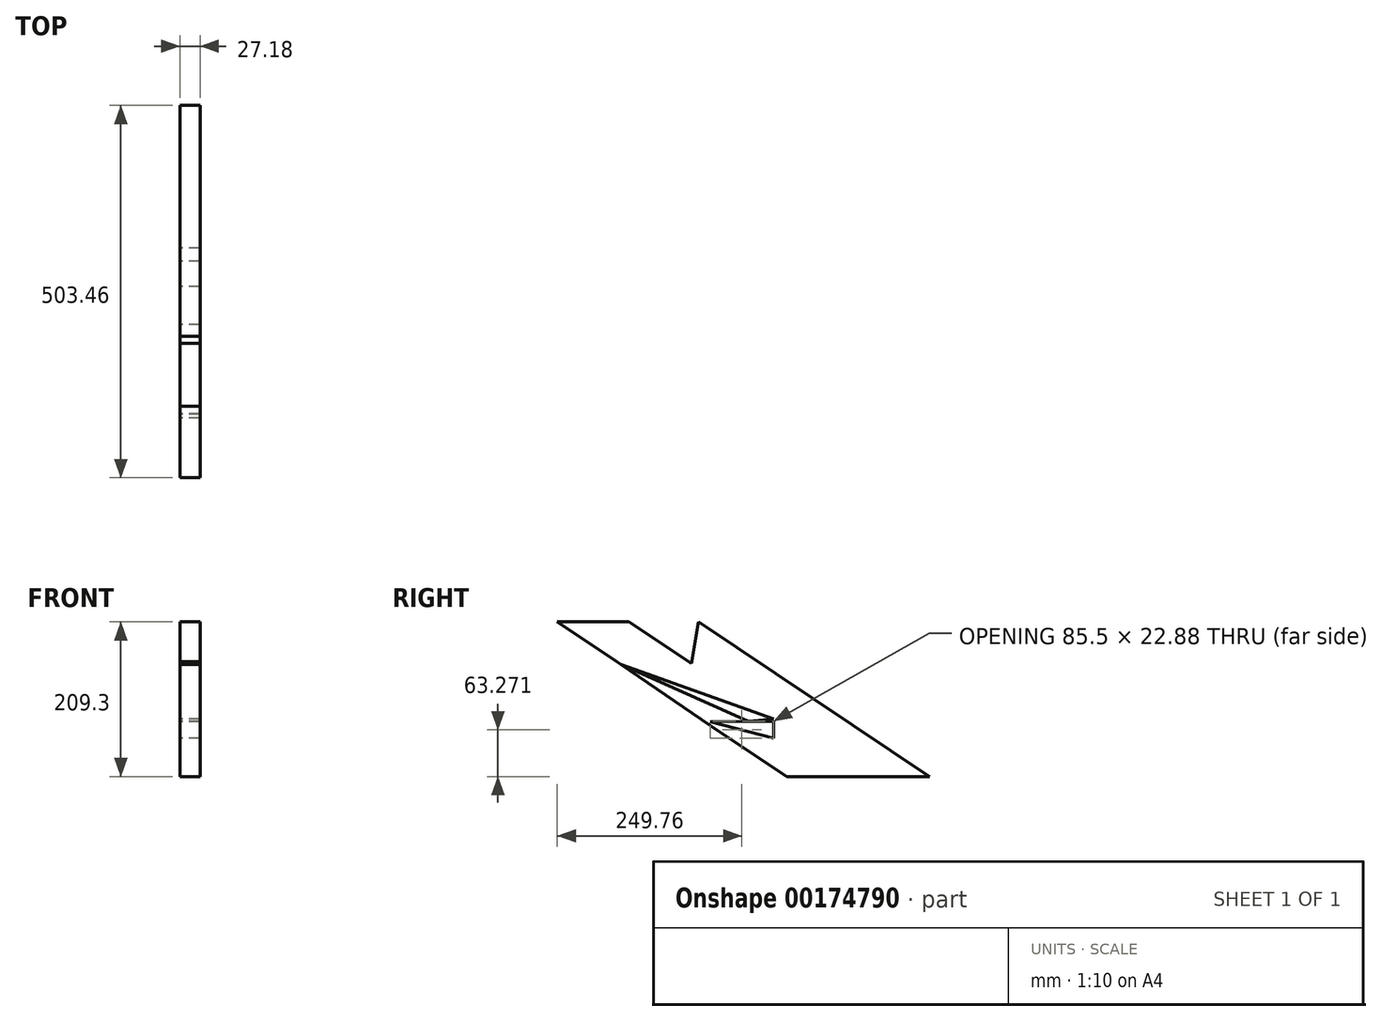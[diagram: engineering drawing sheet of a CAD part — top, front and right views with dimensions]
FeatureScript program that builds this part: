
annotation { "Feature Type Name" : "Feature", "Feature Type Description" : "" }
export const myFeature = defineFeature(function(context is Context, id is Id, definition is map)
    precondition{}
    {
        {
            var Q0;
            Q0=qCreatedBy(makeId("Right.planeOp"),FACE);
            var sketch = newSketch(context, id + "F0", { "sketchPlane" : qUnion([Q0])});
            skLineSegment(sketch, "E0", {"start": v(-206.47, 74.06) * mm, "end": v(-292.5, 131.66) * mm});
            skLineSegment(sketch, "E1", {"start": v(-292.5, 131.66) * mm, "end": v(-195.72, 131.66) * mm});
            skLineSegment(sketch, "E2", {"start": v(-195.72, 131.66) * mm, "end": v(-111.11, 75.01) * mm});
            skLineSegment(sketch, "E3", {"start": v(-111.11, 75.01) * mm, "end": v(-206.47, 74.06) * mm});
            skLineSegment(sketch, "E4", {"start": v(-206.47, 74.06) * mm, "end": v(-195.72, 131.66) * mm});
            skLineSegment(sketch, "E5", {"start": v(-292.5, 131.66) * mm, "end": v(-111.11, 75.01) * mm});
            skLineSegment(sketch, "E6", {"start": v(-195.72, 131.66) * mm, "end": v(-101.62, 131.66) * mm});
            skLineSegment(sketch, "E7", {"start": v(-101.62, 131.66) * mm, "end": v(-111.11, 75.01) * mm});
            skLineSegment(sketch, "E8", {"start": v(-110.23, 73.12) * mm, "end": v(-16.55, 74.06) * mm});
            skLineSegment(sketch, "E9", {"start": v(-16.55, 74.06) * mm, "end": v(0, 0) * mm});
            skLineSegment(sketch, "E10", {"start": v(0, 0) * mm, "end": v(-206.47, 74.06) * mm});
            skLineSegment(sketch, "E11", {"start": v(-206.47, 74.06) * mm, "end": v(-33.87, -2.93) * mm});
            skLineSegment(sketch, "E12", {"start": v(-33.87, -2.93) * mm, "end": v(0, 0) * mm});
            skLineSegment(sketch, "E13", {"start": v(0, -2.93) * mm, "end": v(-85.5, -3.79) * mm});
            skLineSegment(sketch, "E14", {"start": v(-85.5, -3.79) * mm, "end": v(0, -25.8) * mm});
            skLineSegment(sketch, "E15", {"start": v(0, -25.8) * mm, "end": v(0, -2.93) * mm});
            skLineSegment(sketch, "E16", {"start": v(-101.62, 131.66) * mm, "end": v(210.95, -77.64) * mm});
            skLineSegment(sketch, "E17", {"start": v(210.95, -77.64) * mm, "end": v(0, 0) * mm});
            skLineSegment(sketch, "E18", {"start": v(0, -25.8) * mm, "end": v(17.74, -77.64) * mm});
            skLineSegment(sketch, "E19", {"start": v(17.74, -77.64) * mm, "end": v(210.95, -77.64) * mm});
            skLineSegment(sketch, "E20", {"start": v(-85.5, -3.79) * mm, "end": v(-211.78, 77.6) * mm});
            skLineSegment(sketch, "E21", {"start": v(-211.78, 77.6) * mm, "end": v(-348.92, 169.44) * mm});
            skLineSegment(sketch, "E22", {"start": v(-348.92, 169.44) * mm, "end": v(-101.62, 131.66) * mm});
            skLineSegment(sketch, "E23", {"start": v(-85.5, -8.3) * mm, "end": v(17.74, -77.64) * mm});
            skLineSegment(sketch, "E24", {"start": v(-85.5, -8.3) * mm, "end": v(-206.47, 74.06) * mm});
            skLineSegment(sketch, "E25", {"start": v(-155.4, 169.44) * mm, "end": v(-348.92, 169.44) * mm});
            skLineSegment(sketch, "E26", {"start": v(-155.4, 169.44) * mm, "end": v(-101.62, 131.66) * mm});
            skSolve(sketch);
        }
        {
            var Q0;
            {var subQ0=sQuery(id+"F0.wireOp",EDGE,"E2");Q0=makeQuery(id+"F0.imprint","IMPRINT",FACE,{"disambiguationData":[TD([[makeQuery(id+"F0.imprint","IMPRINT",EDGE,{"derivedFrom":subQ0}),-1.0]])]});}
            var Q1;
            {var subQ4=sQuery(id+"F0.wireOp",EDGE,"E7");Q1=makeQuery(id+"F0.imprint","IMPRINT",FACE,{"disambiguationData":[TD([[makeQuery(id+"F0.imprint","IMPRINT",EDGE,{"derivedFrom":subQ4}),1.0]])]});}
            var Q2;
            {var subQ3=sQuery(id+"F0.wireOp",EDGE,"E20");var subQ5=sQuery(id+"F0.wireOp",EDGE,"E4");var subQ6=makeQuery(id+"F0.imprint","INTERSECT",VERTEX,{"derivedFrom":[subQ5,subQ3]});Q2=makeQuery(id+"F0.imprint","IMPRINT",FACE,{"disambiguationData":[TD([[makeQuery(id+"F0.imprint","IMPRINT",EDGE,{"disambiguationData":[TD([[subQ6,-1.0]])],"derivedFrom":subQ5}),-1.0]])]});}
            var Q3;
            {var subQ1=sQuery(id+"F0.wireOp",EDGE,"E14");Q3=makeQuery(id+"F0.imprint","IMPRINT",FACE,{"disambiguationData":[TD([[makeQuery(id+"F0.imprint","IMPRINT",EDGE,{"derivedFrom":subQ1}),-1.0]])]});}
            var Q4;
            {var subQ1=sQuery(id+"F0.wireOp",EDGE,"E12");Q4=makeQuery(id+"F0.imprint","IMPRINT",FACE,{"disambiguationData":[TD([[makeQuery(id+"F0.imprint","IMPRINT",EDGE,{"derivedFrom":subQ1}),-1.0]])]});}
            var Q5;
            {var subQ0=sQuery(id+"F0.wireOp",EDGE,"E20");var subQ1=sQuery(id+"F0.wireOp",EDGE,"E4");var subQ2=makeQuery(id+"F0.imprint","INTERSECT",VERTEX,{"derivedFrom":[subQ1,subQ0]});Q5=makeQuery(id+"F0.imprint","IMPRINT",FACE,{"disambiguationData":[TD([[makeQuery(id+"F0.imprint","IMPRINT",EDGE,{"disambiguationData":[TD([[subQ2,-1.0]])],"derivedFrom":subQ1}),1.0]])]});}
            var Q6;
            {var subQ0=sQuery(id+"F0.wireOp",EDGE,"E1");Q6=makeQuery(id+"F0.imprint","IMPRINT",FACE,{"disambiguationData":[TD([[makeQuery(id+"F0.imprint","IMPRINT",EDGE,{"derivedFrom":subQ0}),-1.0]])]});}
            extrude(context, id + "F1", {"entities" : qUnion([Q0, Q1, Q2, Q3, Q4, Q5, Q6]), "depth" : 27.18 * mm});
        }
    });
